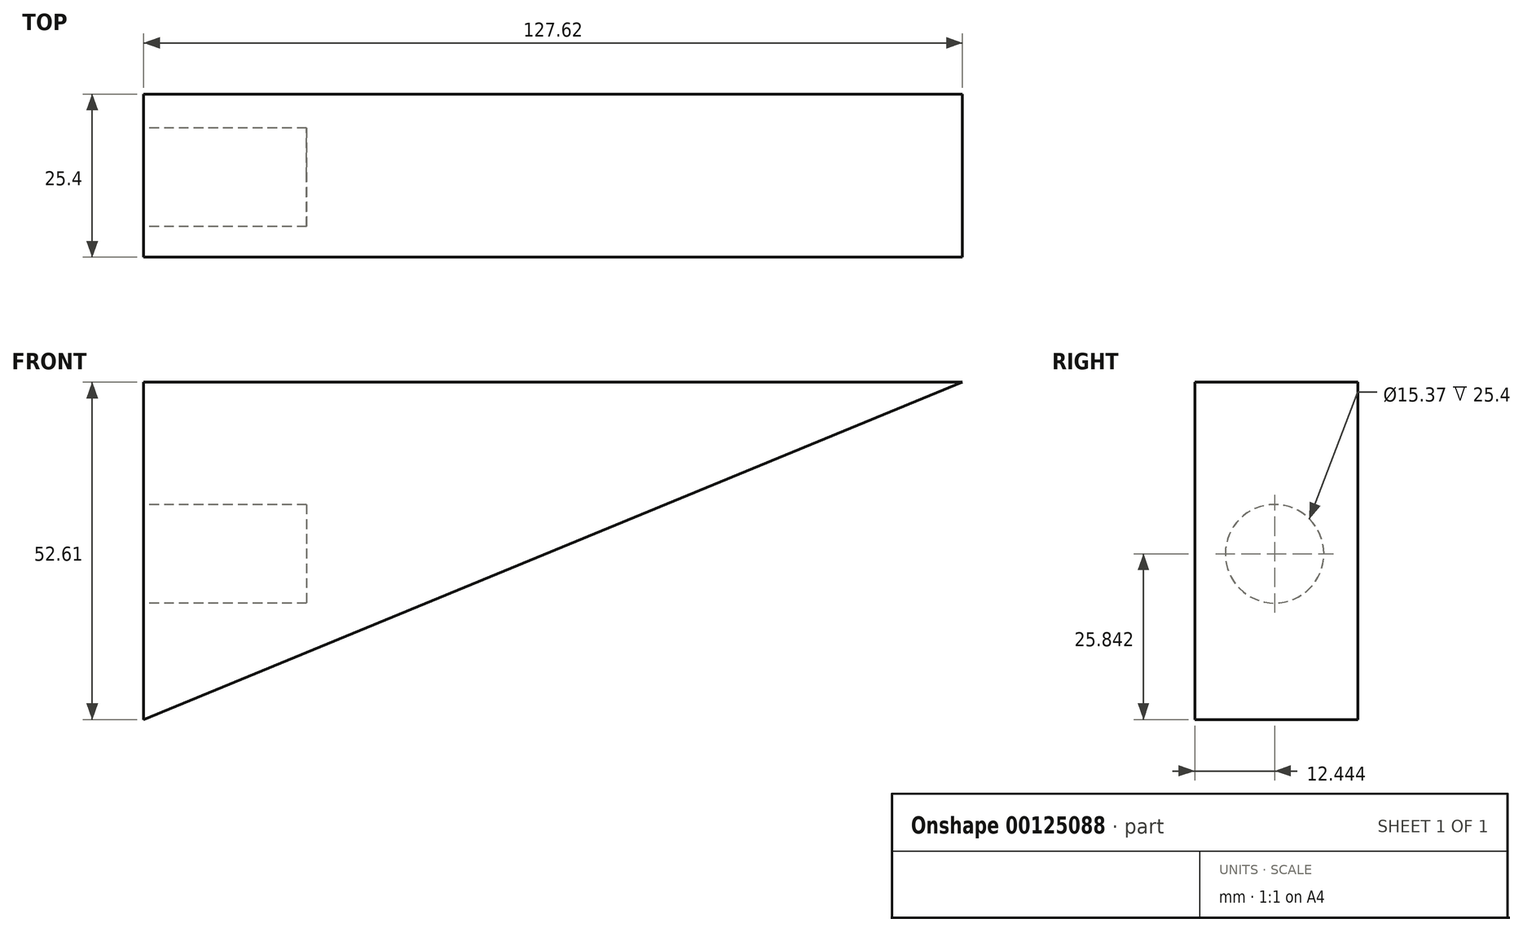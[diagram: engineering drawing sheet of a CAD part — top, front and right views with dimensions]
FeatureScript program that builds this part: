
annotation { "Feature Type Name" : "Feature", "Feature Type Description" : "" }
export const myFeature = defineFeature(function(context is Context, id is Id, definition is map)
    precondition{}
    {
        {
            var Q0;
            Q0=qCreatedBy(makeId("Front.planeOp"),FACE);
            var sketch = newSketch(context, id + "F0", { "sketchPlane" : qUnion([Q0])});
            skLineSegment(sketch, "E0", {"start": v(0, 0) * mm, "end": v(127.62, 0) * mm});
            skLineSegment(sketch, "E1", {"start": v(127.62, 0) * mm, "end": v(0, -52.6) * mm});
            skLineSegment(sketch, "E2", {"start": v(0, -52.6) * mm, "end": v(0, 0) * mm});
            skSolve(sketch);
        }
        {
            var Q0;
            Q0=makeQuery(id+"F0.imprint","IMPRINT",FACE,{"disambiguationData":[TD([[makeQuery(id+"F0.imprint","IMPRINT",EDGE,{"derivedFrom":sQuery(id+"F0.wireOp",EDGE,"E0")}),-1.0]])]});
            var sketch = newSketch(context, id + "F1", { "sketchPlane" : qUnion([Q0])});
            skSolve(sketch);
        }
        {
            var Q0;
            Q0 = qSketchRegion(id + "F1", true);
            var Q1;
            Q1=makeQuery(id+"F0.imprint","IMPRINT",FACE,{"disambiguationData":[TD([[makeQuery(id+"F0.imprint","IMPRINT",EDGE,{"derivedFrom":sQuery(id+"F0.wireOp",EDGE,"E0")}),-1.0]])]});
            extrude(context, id + "F2", {"entities" : qUnion([Q0, Q1]), "depth" : 25.4 * mm});
        }
        {
            var Q0;
            Q0=makeQuery(id+"F2.opExtrude","SWEPT_FACE",FACE,{"disambiguationData":[OSD([sQuery(id+"F0.wireOp",EDGE,"E2")])]});
            var sketch = newSketch(context, id + "F3", { "sketchPlane" : qUnion([Q0])});
            skCircle(sketch, "E3", {"center": v(12.96, -26.77) * mm, "radius": 7.68 * mm});
            skSolve(sketch);
        }
        {
            var Q0;
            Q0=makeQuery(id+"F3.imprint","IMPRINT",FACE,{"disambiguationData":[TD([[makeQuery(id+"F3.imprint","IMPRINT",EDGE,{"derivedFrom":sQuery(id+"F3.wireOp",EDGE,"E3")}),1.0]])]});
            extrude(context, id + "F4", {"entities" : qUnion([Q0]), "operationType" : NewBodyOperationType.REMOVE, "oppositeDirection" : true, "depth" : 25.4 * mm});
        }
    });
